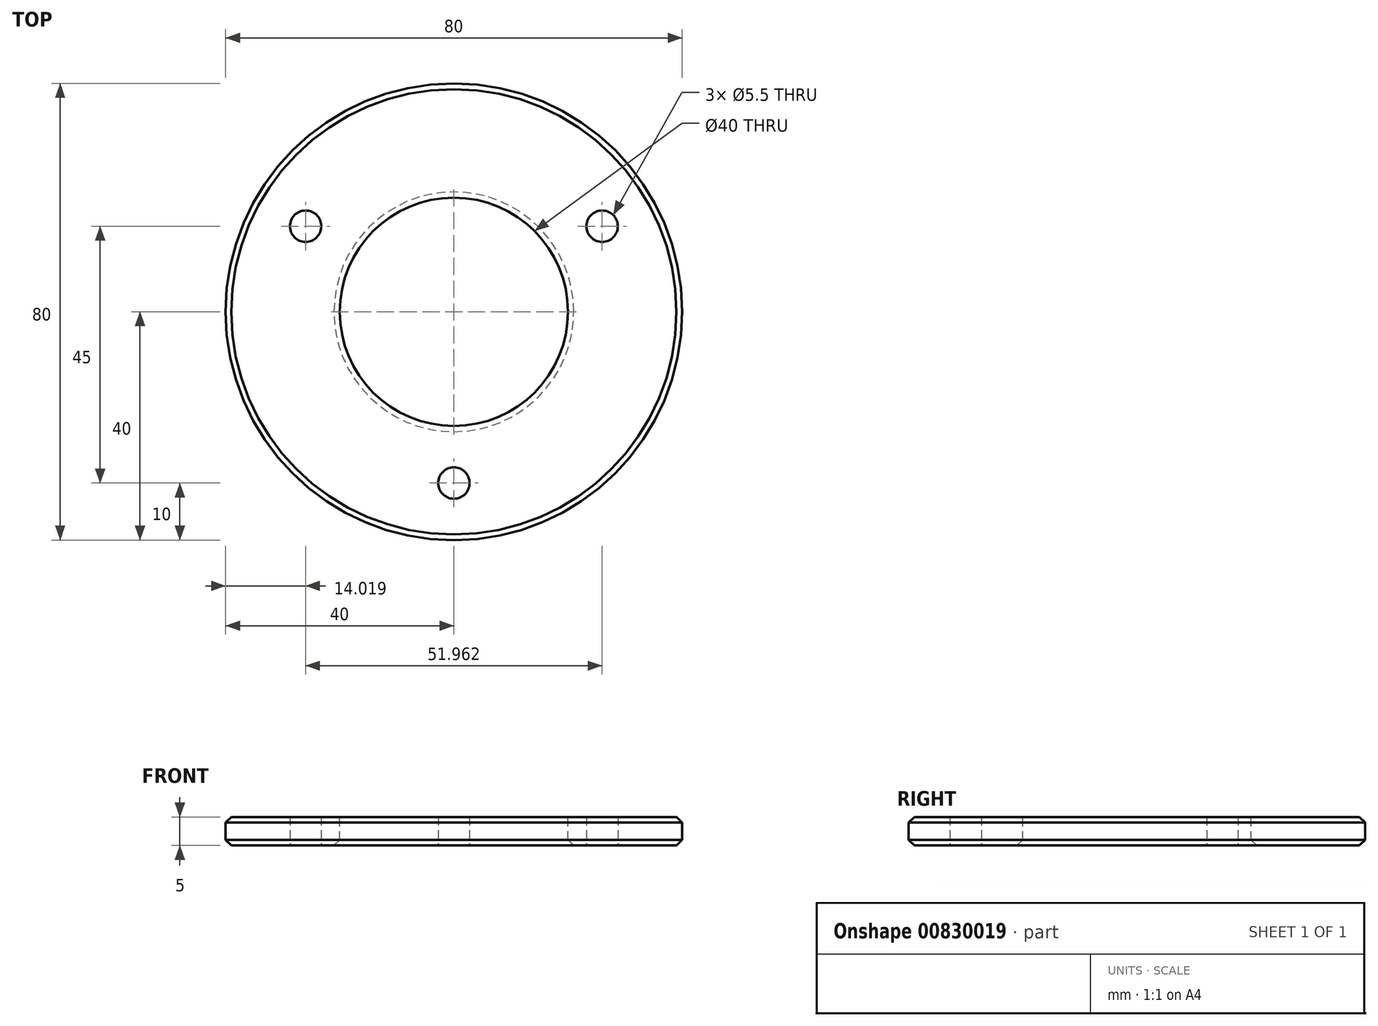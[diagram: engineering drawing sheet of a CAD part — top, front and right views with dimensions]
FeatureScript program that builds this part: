
annotation { "Feature Type Name" : "Feature", "Feature Type Description" : "" }
export const myFeature = defineFeature(function(context is Context, id is Id, definition is map)
    precondition{}
    {
        {
            var Q0;
            Q0=qCreatedBy(makeId("Top.planeOp"),FACE);
            var sketch = newSketch(context, id + "F0", { "sketchPlane" : qUnion([Q0])});
            skCircle(sketch, "E0", {"center": v(0, 0) * mm, "radius": 40 * mm});
            skSolve(sketch);
        }
        {
            var Q0;
            Q0=makeQuery(id+"F0.imprint","IMPRINT",FACE,{"disambiguationData":[TD([[makeQuery(id+"F0.imprint","IMPRINT",EDGE,{"derivedFrom":sQuery(id+"F0.wireOp",EDGE,"E0")}),1.0]])]});
            extrude(context, id + "F1", {"entities" : qUnion([Q0]), "depth" : 5 * mm, "offsetDistance" : 25 * mm});
        }
        {
            var Q0;
            Q0=makeQuery(id+"F1.opExtrude","CAP_FACE",FACE,{"disambiguationData":[OSD([sQuery(id+"F0.wireOp",EDGE,"E0")])],"isStart":true});
            var sketch = newSketch(context, id + "F2", { "sketchPlane" : qUnion([Q0])});
            skCircle(sketch, "E1", {"center": v(0, 0) * mm, "radius": 30 * mm, "construction": true});
            skPoint(sketch, "E2", {"position": v(0, 30) * mm});
            skLineSegment(sketch, "E3", {"start": v(0, 0) * mm, "end": v(0, 30) * mm, "construction": true});
            skLineSegment(sketch, "E4", {"start": v(0, 0) * mm, "end": v(25.98, -15) * mm, "construction": true});
            skLineSegment(sketch, "E5", {"start": v(-25.98, -15) * mm, "end": v(0, 0) * mm, "construction": true});
            skSolve(sketch);
        }
        {
            var Q0;
            Q0=sQuery(id+"F2.wireOp",VERTEX,"E2");
            var Q1;
            Q1=sQuery(id+"F2.wireOp",VERTEX,"E4.end");
            var Q2;
            Q2=sQuery(id+"F2.wireOp",VERTEX,"E5.start");
            var Q3;
            Q3=makeQuery(id+"F1.opExtrude","SWEPT_BODY",BODY,{"disambiguationData":[OSD([sQuery(id+"F0.wireOp",EDGE,"E0")])]});
            hole(context, id + "F3", {"style" : HoleStyle.SIMPLE, "endStyle" : HoleEndStyle.THROUGH, "holeDiameter" : 5.5 * mm, "majorDiameter" : 5 * mm, "isTappedThrough" : true, "tappedDepth" : 12 * mm, "tapClearance" : 3, "locations" : qUnion([Q0, Q1, Q2]), "scope" : qUnion([Q3])});
        }
        {
            var Q0;
            Q0=makeQuery(id+"F1.opExtrude","CAP_FACE",FACE,{"disambiguationData":[OSD([sQuery(id+"F0.wireOp",EDGE,"E0")])],"isStart":false});
            var sketch = newSketch(context, id + "F4", { "sketchPlane" : qUnion([Q0])});
            skCircle(sketch, "E6", {"center": v(0, 0) * mm, "radius": 20 * mm});
            skSolve(sketch);
        }
        {
            var Q0;
            Q0=makeQuery(id+"F4.imprint","IMPRINT",FACE,{"disambiguationData":[TD([[makeQuery(id+"F4.imprint","IMPRINT",EDGE,{"derivedFrom":sQuery(id+"F4.wireOp",EDGE,"E6")}),1.0]])]});
            extrude(context, id + "F5", {"entities" : qUnion([Q0]), "operationType" : NewBodyOperationType.REMOVE, "endBound" : BoundingType.THROUGH_ALL, "oppositeDirection" : true, "depth" : 25 * mm, "offsetDistance" : 25 * mm});
        }
        {
            var Q0;
            Q0=makeQuery(id+"F1.opExtrude","CAP_EDGE",EDGE,{"disambiguationData":[OSD([sQuery(id+"F0.wireOp",EDGE,"E0")])],"isStart":false});
            var Q1;
            Q1=makeQuery(id+"F1.opExtrude","CAP_EDGE",EDGE,{"disambiguationData":[OSD([sQuery(id+"F0.wireOp",EDGE,"E0")])],"isStart":true});
            var Q2;
            Q2=makeQuery(id+"F5.boolean.opBoolean","COPY",EDGE,{"derivedFrom":makeQuery(id+"F5.opExtrude","CAP_EDGE",EDGE,{"disambiguationData":[OSD([sQuery(id+"F4.wireOp",EDGE,"E6")])],"isStart":true})});
            var Q3;
            Q3=makeQuery(id+"F5.boolean.opBoolean","INTERSECT",EDGE,{"derivedFrom":[makeQuery(id+"F1.opExtrude","CAP_FACE",FACE,{"disambiguationData":[OSD([sQuery(id+"F0.wireOp",EDGE,"E0")])],"isStart":true}),makeQuery(id+"F5.opExtrude","SWEPT_FACE",FACE,{"disambiguationData":[OSD([sQuery(id+"F4.wireOp",EDGE,"E6")])]})]});
            chamfer(context, id + "F6", {"entities" : qUnion([Q0, Q1, Q2, Q3]), "width" : 1 * mm, "tangentPropagation" : true});
        }
    });
